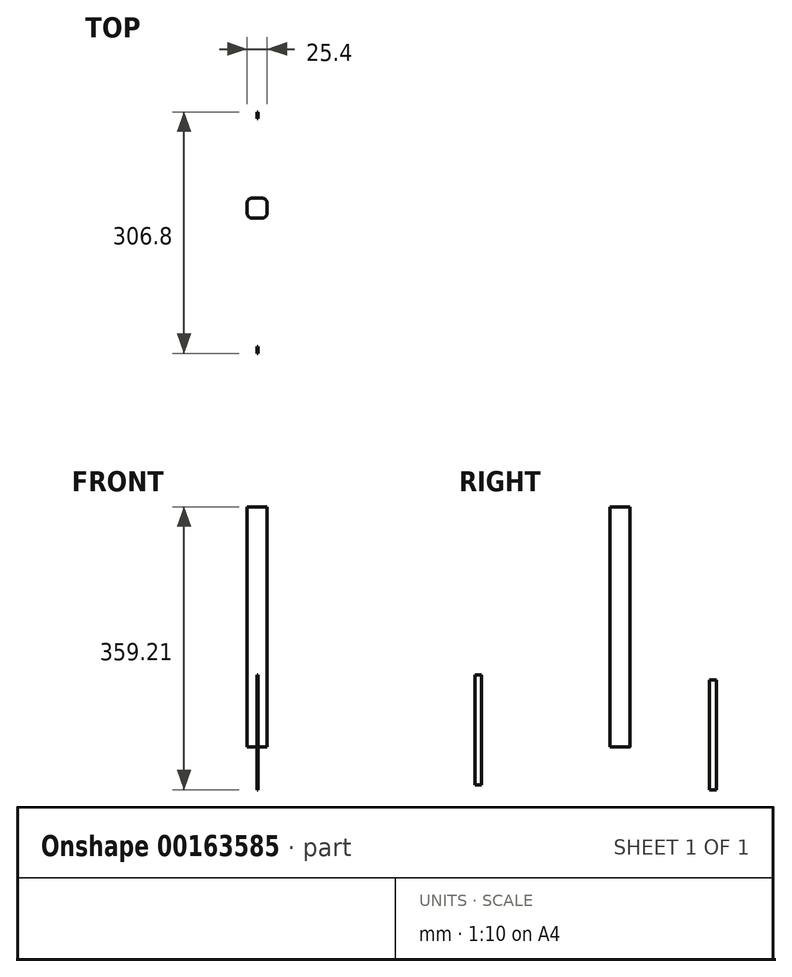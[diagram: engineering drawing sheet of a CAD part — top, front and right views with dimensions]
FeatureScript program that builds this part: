
annotation { "Feature Type Name" : "Feature", "Feature Type Description" : "" }
export const myFeature = defineFeature(function(context is Context, id is Id, definition is map)
    precondition{}
    {
        {
            var Q0;
            Q0=qCreatedBy(makeId("Top.planeOp"),FACE);
            var sketch = newSketch(context, id + "F0", { "sketchPlane" : qUnion([Q0])});
            skLineSegment(sketch, "E0.bottom", {"start": v(6.35, 12.7) * mm, "end": v(-6.35, 12.7) * mm});
            skLineSegment(sketch, "E0.top", {"start": v(6.35, -12.7) * mm, "end": v(-6.35, -12.7) * mm});
            skLineSegment(sketch, "E0.left", {"start": v(12.7, 6.35) * mm, "end": v(12.7, -6.35) * mm});
            skLineSegment(sketch, "E0.right", {"start": v(-12.7, 6.35) * mm, "end": v(-12.7, -6.35) * mm});
            skPoint(sketch, "E0.middle", {"position": v(0, 0) * mm});
            skPoint(sketch, "E1.visualSharp", {"position": v(-12.7, 12.7) * mm});
            skArc(sketch, "E1.filletArc", {"start": v(-6.35, 12.7) * mm, "mid": v(-10.84, 10.84) * mm, "end": v(-12.7, 6.35) * mm});
            skPoint(sketch, "E2.visualSharp", {"position": v(-12.7, -12.7) * mm});
            skArc(sketch, "E2.filletArc", {"start": v(-12.7, -6.35) * mm, "mid": v(-10.84, -10.84) * mm, "end": v(-6.35, -12.7) * mm});
            skPoint(sketch, "E3.visualSharp", {"position": v(12.7, -12.7) * mm});
            skArc(sketch, "E3.filletArc", {"start": v(6.35, -12.7) * mm, "mid": v(10.84, -10.84) * mm, "end": v(12.7, -6.35) * mm});
            skPoint(sketch, "E4.visualSharp", {"position": v(12.7, 12.7) * mm});
            skArc(sketch, "E4.filletArc", {"start": v(12.7, 6.35) * mm, "mid": v(10.84, 10.84) * mm, "end": v(6.35, 12.7) * mm});
            skSolve(sketch);
        }
        {
            var Q0;
            Q0=qSketchRegion(id+"F0",true);
            extrude(context, id + "F1", {"entities" : qUnion([Q0]), "depth" : 304.8 * mm});
        }
        {
            var Q0;
            Q0=qCreatedBy(makeId("Right.planeOp"),FACE);
            var sketch = newSketch(context, id + "F2", { "sketchPlane" : qUnion([Q0])});
            skLineSegment(sketch, "E5.bottom", {"start": v(-184.56, 91.09) * mm, "end": v(-176.09, 91.09) * mm});
            skLineSegment(sketch, "E5.top", {"start": v(-184.56, -48.61) * mm, "end": v(-176.09, -48.61) * mm});
            skLineSegment(sketch, "E5.left", {"start": v(-184.56, 91.09) * mm, "end": v(-184.56, -48.61) * mm});
            skLineSegment(sketch, "E5.right", {"start": v(-176.09, 91.09) * mm, "end": v(-176.09, -48.61) * mm});
            skSolve(sketch);
        }
        {
            var Q0;
            Q0 = qSketchRegion(id + "F2", true);
            extrude(context, id + "F3", {"entities" : qUnion([Q0]), "depth" : 1.27 * mm});
        }
        {
            var Q0;
            Q0=qCreatedBy(makeId("Right.planeOp"),FACE);
            var sketch = newSketch(context, id + "F4", { "sketchPlane" : qUnion([Q0])});
            skLineSegment(sketch, "E6.bottom", {"start": v(113.78, 85.29) * mm, "end": v(122.24, 85.29) * mm});
            skLineSegment(sketch, "E6.top", {"start": v(113.78, -54.41) * mm, "end": v(122.24, -54.41) * mm});
            skLineSegment(sketch, "E6.left", {"start": v(113.78, 85.29) * mm, "end": v(113.78, -54.41) * mm});
            skLineSegment(sketch, "E6.right", {"start": v(122.24, 85.29) * mm, "end": v(122.24, -54.41) * mm});
            skSolve(sketch);
        }
        {
            var Q0;
            Q0 = qSketchRegion(id + "F4", true);
            extrude(context, id + "F5", {"entities" : qUnion([Q0]), "depth" : 1.27 * mm});
        }
    });
